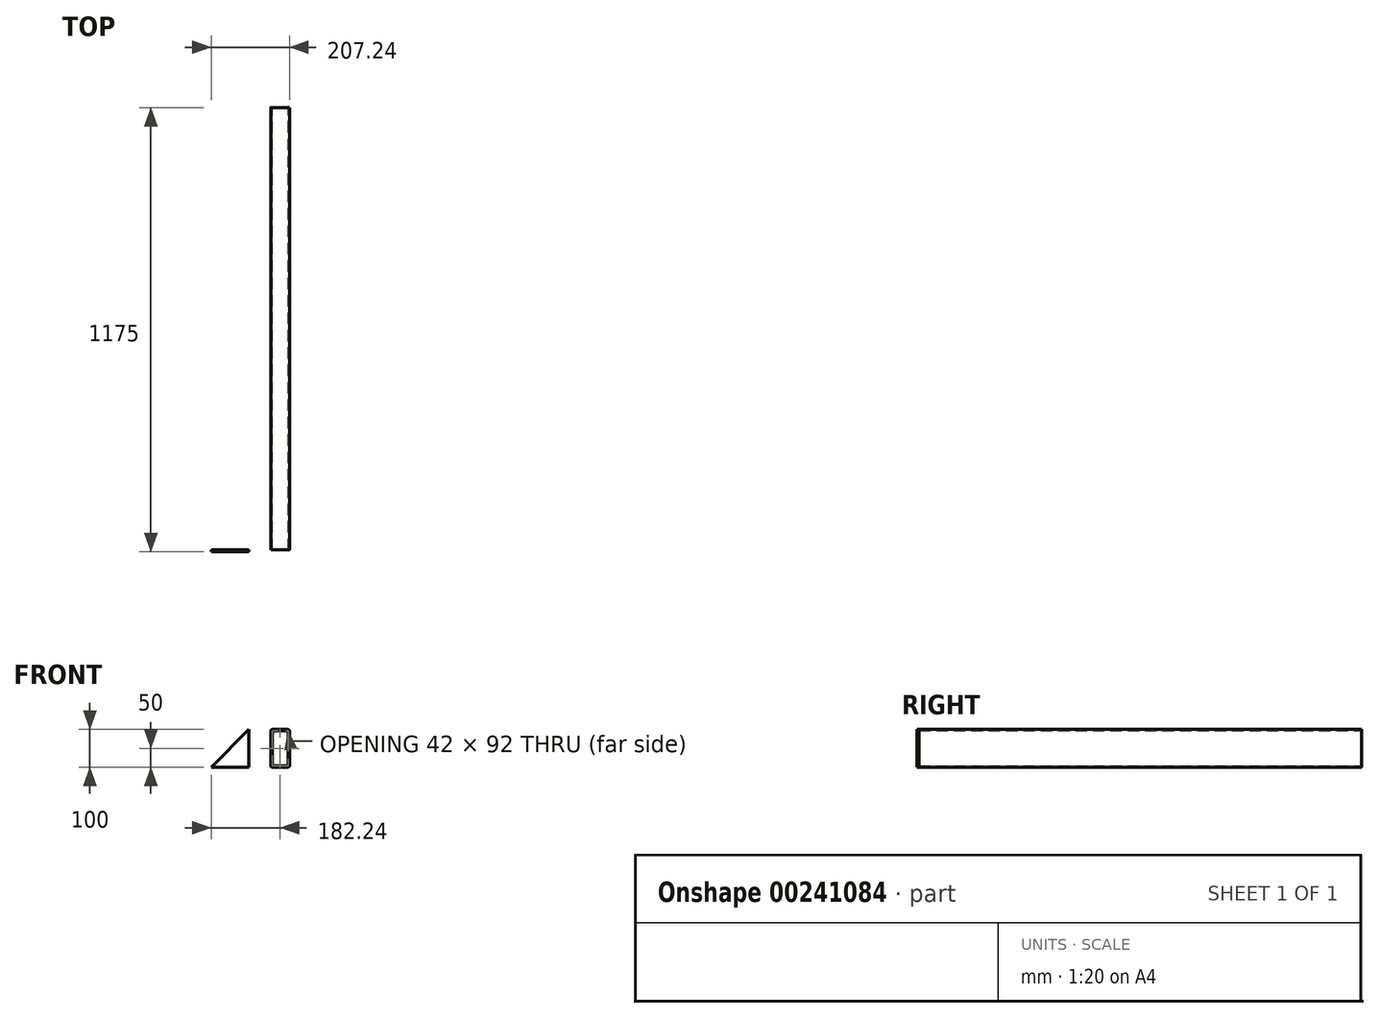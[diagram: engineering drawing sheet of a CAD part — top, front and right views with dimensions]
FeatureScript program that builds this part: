
annotation { "Feature Type Name" : "Feature", "Feature Type Description" : "" }
export const myFeature = defineFeature(function(context is Context, id is Id, definition is map)
    precondition{}
    {
        {
            var Q0;
            Q0=qCreatedBy(makeId("Top.planeOp"),FACE);
            var sketch = newSketch(context, id + "F0", { "sketchPlane" : qUnion([Q0])});
            skLineSegment(sketch, "E0.bottom", {"start": v(0, 0) * mm, "end": v(50, 0) * mm});
            skLineSegment(sketch, "E0.top", {"start": v(0, 1170) * mm, "end": v(50, 1170) * mm});
            skLineSegment(sketch, "E0.left", {"start": v(0, 0) * mm, "end": v(0, 1170) * mm});
            skLineSegment(sketch, "E0.right", {"start": v(50, 0) * mm, "end": v(50, 1170) * mm});
            skSolve(sketch);
        }
        {
            var Q0;
            Q0=makeQuery(id+"F0.imprint","IMPRINT",FACE,{"disambiguationData":[TD([[makeQuery(id+"F0.imprint","IMPRINT",EDGE,{"derivedFrom":sQuery(id+"F0.wireOp",EDGE,"E0.bottom")}),1.0]])]});
            extrude(context, id + "F1", {"entities" : qUnion([Q0]), "depth" : 100 * mm});
        }
        {
            var Q0;
            Q0=makeQuery(id+"F1.opExtrude","CAP_EDGE",EDGE,{"disambiguationData":[OSD([sQuery(id+"F0.wireOp",EDGE,"E0.right")])],"isStart":false});
            var Q1;
            Q1=makeQuery(id+"F1.opExtrude","CAP_EDGE",EDGE,{"disambiguationData":[OSD([sQuery(id+"F0.wireOp",EDGE,"E0.left")])],"isStart":false});
            var Q2;
            Q2=makeQuery(id+"F1.opExtrude","CAP_EDGE",EDGE,{"disambiguationData":[OSD([sQuery(id+"F0.wireOp",EDGE,"E0.right")])],"isStart":true});
            var Q3;
            Q3=makeQuery(id+"F1.opExtrude","CAP_EDGE",EDGE,{"disambiguationData":[OSD([sQuery(id+"F0.wireOp",EDGE,"E0.left")])],"isStart":true});
            fillet(context, id + "F2", {"entities" : qUnion([Q0, Q1, Q2, Q3]), "radius" : 5 * mm, "tangentPropagation" : true, "allowEdgeOverflow" : false});
        }
        {
            var Q0;
            Q0=makeQuery(id+"F1.opExtrude","SWEPT_FACE",FACE,{"disambiguationData":[OSD([sQuery(id+"F0.wireOp",EDGE,"E0.bottom")])]});
            var Q1;
            Q1=makeQuery(id+"F1.opExtrude","SWEPT_FACE",FACE,{"disambiguationData":[OSD([sQuery(id+"F0.wireOp",EDGE,"E0.top")])]});
            shell(context, id + "F3", {"entities" : qUnion([Q0, Q1]), "thickness" : 4 * mm});
        }
        {
            var Q0;
            Q0=qCreatedBy(makeId("Front.planeOp"),FACE);
            var sketch = newSketch(context, id + "F4", { "sketchPlane" : qUnion([Q0])});
            skLineSegment(sketch, "E1", {"start": v(-57.24, 0) * mm, "end": v(-57.24, 100) * mm});
            skLineSegment(sketch, "E2", {"start": v(-57.24, 100) * mm, "end": v(-157.24, 0) * mm});
            skLineSegment(sketch, "E3", {"start": v(-157.24, 0) * mm, "end": v(-57.24, 0) * mm});
            skSolve(sketch);
        }
        {
            var Q0;
            Q0=makeQuery(id+"F4.imprint","IMPRINT",FACE,{"disambiguationData":[TD([[makeQuery(id+"F4.imprint","IMPRINT",EDGE,{"derivedFrom":sQuery(id+"F4.wireOp",EDGE,"E1")}),1.0]])]});
            extrude(context, id + "F5", {"entities" : qUnion([Q0]), "depth" : 5 * mm});
        }
    });
